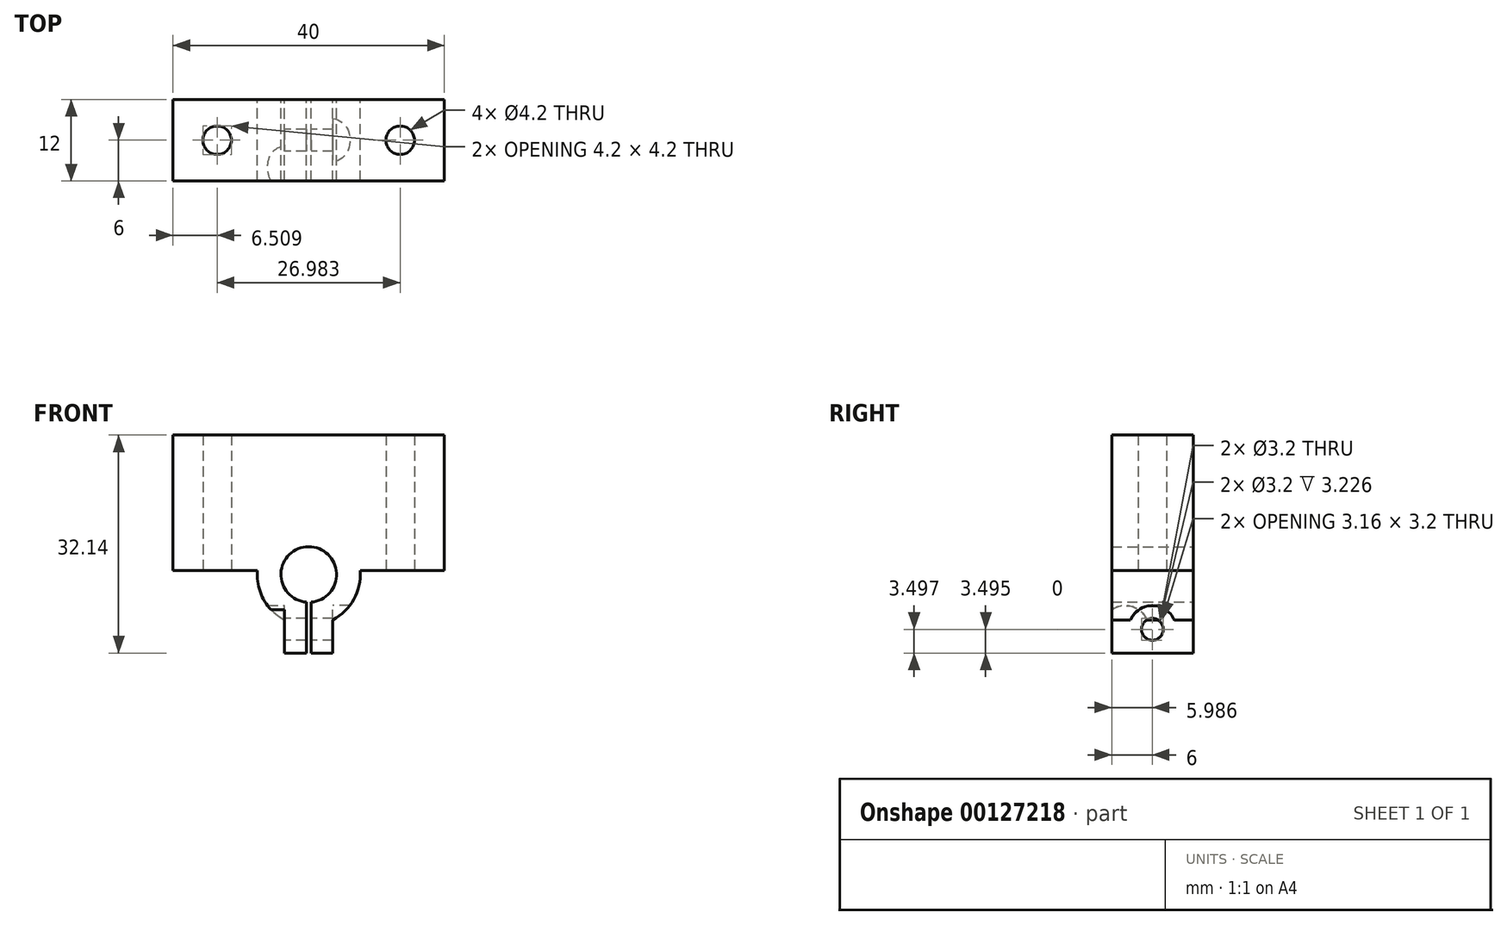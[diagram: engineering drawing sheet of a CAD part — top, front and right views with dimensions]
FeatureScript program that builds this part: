
annotation { "Feature Type Name" : "Feature", "Feature Type Description" : "" }
export const myFeature = defineFeature(function(context is Context, id is Id, definition is map)
    precondition{}
    {
        {
            var Q0;
            Q0=qCreatedBy(makeId("Front.planeOp"),FACE);
            var sketch = newSketch(context, id + "F0", { "sketchPlane" : qUnion([Q0])});
            skArc(sketch, "E0", {"start": v(0.34, -4.09) * mm, "mid": v(0, 4.1) * mm, "end": v(-0.34, -4.09) * mm});
            skLineSegment(sketch, "E1", {"start": v(-4.1, 0) * mm, "end": v(-7.6, 0) * mm});
            skLineSegment(sketch, "E2", {"start": v(4.1, 0) * mm, "end": v(7.6, 0) * mm});
            skArc(sketch, "E3", {"start": v(3.56, -6.71) * mm, "mid": v(0, 7.6) * mm, "end": v(-3.56, -6.71) * mm});
            skLineSegment(sketch, "E4", {"start": v(0, 0) * mm, "end": v(0, 3) * mm});
            skLineSegment(sketch, "E5", {"start": v(-2.8, 3) * mm, "end": v(-20, 3) * mm});
            skLineSegment(sketch, "E6", {"start": v(2.8, 3) * mm, "end": v(20, 3) * mm});
            skLineSegment(sketch, "E7", {"start": v(-20, 3) * mm, "end": v(-20, 13) * mm});
            skLineSegment(sketch, "E8", {"start": v(-20, 13) * mm, "end": v(20, 13) * mm});
            skLineSegment(sketch, "E9", {"start": v(20, 13) * mm, "end": v(20, 3) * mm});
            skLineSegment(sketch, "E10", {"start": v(0, 0) * mm, "end": v(-0.5, 0) * mm});
            skLineSegment(sketch, "E11", {"start": v(0, 0) * mm, "end": v(0.5, 0) * mm});
            skLineSegment(sketch, "E12", {"start": v(3.56, -11.6) * mm, "end": v(3.56, -6.71) * mm});
            skLineSegment(sketch, "E13", {"start": v(-3.56, -11.6) * mm, "end": v(-3.56, -6.71) * mm});
            skLineSegment(sketch, "E14", {"start": v(-0.34, -4.09) * mm, "end": v(-0.34, -11.6) * mm});
            skLineSegment(sketch, "E15", {"start": v(0.34, -4.09) * mm, "end": v(0.34, -11.6) * mm});
            skLineSegment(sketch, "E16", {"start": v(0.34, -11.6) * mm, "end": v(3.56, -11.6) * mm});
            skLineSegment(sketch, "E17", {"start": v(-0.34, -11.6) * mm, "end": v(-3.56, -11.6) * mm});
            skSolve(sketch);
        }
        {
            var Q0;
            Q0=qSketchRegion(id+"F0",true);
            extrude(context, id + "F1", {"entities" : qUnion([Q0]), "depth" : 12 * mm});
        }
        {
            var Q0;
            Q0=makeQuery(id+"F1.opExtrude","SWEPT_FACE",FACE,{"disambiguationData":[OSD([sQuery(id+"F0.wireOp",EDGE,"E5")])]});
            var sketch = newSketch(context, id + "F2", { "sketchPlane" : qUnion([Q0])});
            skLineSegment(sketch, "E18", {"start": v(-13.5, 12) * mm, "end": v(-13.5, 0) * mm});
            skCircle(sketch, "E19", {"center": v(-13.5, 6) * mm, "radius": 2.1 * mm});
            skSolve(sketch);
        }
        {
            var Q0;
            Q0=qSketchRegion(id+"F2",true);
            extrude(context, id + "F3", {"entities" : qUnion([Q0]), "operationType" : NewBodyOperationType.REMOVE, "oppositeDirection" : true, "depth" : 25 * mm});
        }
        {
            var Q0;
            Q0=makeQuery(id+"F1.opExtrude","SWEPT_FACE",FACE,{"disambiguationData":[OSD([sQuery(id+"F0.wireOp",EDGE,"E6")])]});
            var sketch = newSketch(context, id + "F4", { "sketchPlane" : qUnion([Q0])});
            skLineSegment(sketch, "E20", {"start": v(13.5, 12) * mm, "end": v(13.5, 0) * mm});
            skCircle(sketch, "E21", {"center": v(13.5, 6) * mm, "radius": 2.1 * mm});
            skSolve(sketch);
        }
        {
            var Q0;
            Q0=qSketchRegion(id+"F4",true);
            extrude(context, id + "F5", {"entities" : qUnion([Q0]), "operationType" : NewBodyOperationType.REMOVE, "oppositeDirection" : true, "depth" : 25 * mm});
        }
        {
            var Q0;
            Q0=makeQuery(id+"F1.opExtrude","SWEPT_FACE",FACE,{"disambiguationData":[OSD([sQuery(id+"F0.wireOp",EDGE,"E13")])]});
            var sketch = newSketch(context, id + "F6", { "sketchPlane" : qUnion([Q0])});
            skLineSegment(sketch, "E22", {"start": v(6, -11.6) * mm, "end": v(6, -4.6) * mm});
            skCircle(sketch, "E23", {"center": v(6, -8.1) * mm, "radius": 1.6 * mm});
            skSolve(sketch);
        }
        {
            var Q0;
            Q0=qSketchRegion(id+"F6",true);
            extrude(context, id + "F7", {"entities" : qUnion([Q0]), "operationType" : NewBodyOperationType.REMOVE, "oppositeDirection" : true, "depth" : 25 * mm});
        }
        {
            var Q0;
            Q0=makeQuery(id+"F1.opExtrude","SWEPT_FACE",FACE,{"disambiguationData":[OSD([sQuery(id+"F0.wireOp",EDGE,"E13")])]});
            var sketch = newSketch(context, id + "F8", { "sketchPlane" : qUnion([Q0])});
            skCircle(sketch, "E24", {"center": v(10, -8.1) * mm, "radius": 3.5 * mm});
            skSolve(sketch);
        }
        {
            var Q0;
            Q0=qSketchRegion(id+"F8",true);
            extrude(context, id + "F9", {"entities" : qUnion([Q0]), "operationType" : NewBodyOperationType.REMOVE, "depth" : 25 * mm});
        }
        {
            var Q0;
            Q0=makeQuery(id+"F1.opExtrude","SWEPT_FACE",FACE,{"disambiguationData":[OSD([sQuery(id+"F0.wireOp",EDGE,"E12")])]});
            var sketch = newSketch(context, id + "F10", { "sketchPlane" : qUnion([Q0])});
            skCircle(sketch, "E25", {"center": v(-6, -8.1) * mm, "radius": 3.5 * mm});
            skSolve(sketch);
        }
        {
            var Q0;
            Q0=qSketchRegion(id+"F10",true);
            extrude(context, id + "F11", {"entities" : qUnion([Q0]), "operationType" : NewBodyOperationType.REMOVE, "depth" : 25 * mm});
        }
        {
            var Q0;
            Q0=qSketchRegion(id+"F8",true);
            extrude(context, id + "F12", {"entities" : qUnion([Q0]), "operationType" : NewBodyOperationType.REMOVE, "depth" : 25 * mm});
        }
        {
            var Q0;
            Q0=makeQuery(id+"F1.opExtrude","SWEPT_FACE",FACE,{"disambiguationData":[OSD([sQuery(id+"F0.wireOp",EDGE,"E8")])]});
            var sketch = newSketch(context, id + "F13", { "sketchPlane" : qUnion([Q0])});
            skLineSegment(sketch, "E26.bottom", {"start": v(20, -12) * mm, "end": v(-20, -12) * mm});
            skLineSegment(sketch, "E26.top", {"start": v(20, 0) * mm, "end": v(-20, 0) * mm});
            skLineSegment(sketch, "E26.left", {"start": v(20, -12) * mm, "end": v(20, 0) * mm});
            skLineSegment(sketch, "E26.right", {"start": v(-20, -12) * mm, "end": v(-20, 0) * mm});
            skCircle(sketch, "E27", {"center": v(13.5, -6) * mm, "radius": 2.1 * mm});
            skCircle(sketch, "E28", {"center": v(-13.5, -6) * mm, "radius": 2.1 * mm});
            skSolve(sketch);
        }
        {
            var Q0;
            Q0=qSketchRegion(id+"F13",true);
            extrude(context, id + "F14", {"entities" : qUnion([Q0]), "operationType" : NewBodyOperationType.ADD, "depth" : 7.55 * mm});
        }
        {
            var Q0;
            Q0=makeQuery(id+"F1.opExtrude","SWEPT_FACE",FACE,{"disambiguationData":[OSD([sQuery(id+"F0.wireOp",EDGE,"E5")])]});
            var sketch = newSketch(context, id + "F15", { "sketchPlane" : qUnion([Q0])});
            skLineSegment(sketch, "E29.bottom", {"start": v(-20, 12) * mm, "end": v(-6.98, 12) * mm});
            skLineSegment(sketch, "E29.top", {"start": v(-20, 0) * mm, "end": v(-6.98, 0) * mm});
            skLineSegment(sketch, "E29.left", {"start": v(-20, 12) * mm, "end": v(-20, 0) * mm});
            skLineSegment(sketch, "E29.right", {"start": v(-6.98, 12) * mm, "end": v(-6.98, 0) * mm});
            skCircle(sketch, "E30", {"center": v(-13.5, 6) * mm, "radius": 2.1 * mm});
            skSolve(sketch);
        }
        {
            var Q0;
            Q0=makeQuery(id+"F1.opExtrude","SWEPT_FACE",FACE,{"disambiguationData":[OSD([sQuery(id+"F0.wireOp",EDGE,"E6")])]});
            var sketch = newSketch(context, id + "F16", { "sketchPlane" : qUnion([Q0])});
            skLineSegment(sketch, "E31.bottom", {"start": v(20, 12) * mm, "end": v(6.98, 12) * mm});
            skLineSegment(sketch, "E31.top", {"start": v(20, 0) * mm, "end": v(6.98, 0) * mm});
            skLineSegment(sketch, "E31.left", {"start": v(20, 12) * mm, "end": v(20, 0) * mm});
            skLineSegment(sketch, "E31.right", {"start": v(6.98, 12) * mm, "end": v(6.98, 0) * mm});
            skCircle(sketch, "E32", {"center": v(13.5, 6) * mm, "radius": 2.1 * mm});
            skSolve(sketch);
        }
        {
            var Q0;
            Q0=qSketchRegion(id+"F16",true);
            var Q1;
            Q1=makeQuery(id+"F15.imprint","IMPRINT",FACE,{"disambiguationData":[TD([[makeQuery(id+"F15.imprint","IMPRINT",EDGE,{"derivedFrom":sQuery(id+"F15.wireOp",EDGE,"E29.bottom")}),1.0]])]});
            extrude(context, id + "F17", {"entities" : qUnion([Q0, Q1]), "operationType" : NewBodyOperationType.ADD, "depth" : 2.45 * mm});
        }
        {
            var Q0;
            Q0=makeQuery(id+"F1.opExtrude","SWEPT_BODY",BODY,{"disambiguationData":[OSD([sQuery(id+"F0.wireOp",EDGE,"E0"),sQuery(id+"F0.wireOp",EDGE,"E3"),sQuery(id+"F0.wireOp",EDGE,"E5"),sQuery(id+"F0.wireOp",EDGE,"E6"),sQuery(id+"F0.wireOp",EDGE,"E7"),sQuery(id+"F0.wireOp",EDGE,"E8"),sQuery(id+"F0.wireOp",EDGE,"E9"),sQuery(id+"F0.wireOp",EDGE,"E12"),sQuery(id+"F0.wireOp",EDGE,"E13"),sQuery(id+"F0.wireOp",EDGE,"E14"),sQuery(id+"F0.wireOp",EDGE,"E15"),sQuery(id+"F0.wireOp",EDGE,"E16"),sQuery(id+"F0.wireOp",EDGE,"E17")])]});
            transform(context, id + "F18", {"entities" : qUnion([Q0]), "transformType" : TransformType.TRANSLATION_3D, "dx" : 0 * mm, "dy" : 0 * mm, "dz" : 0 * mm, "makeCopy" : true});
        }
    });
